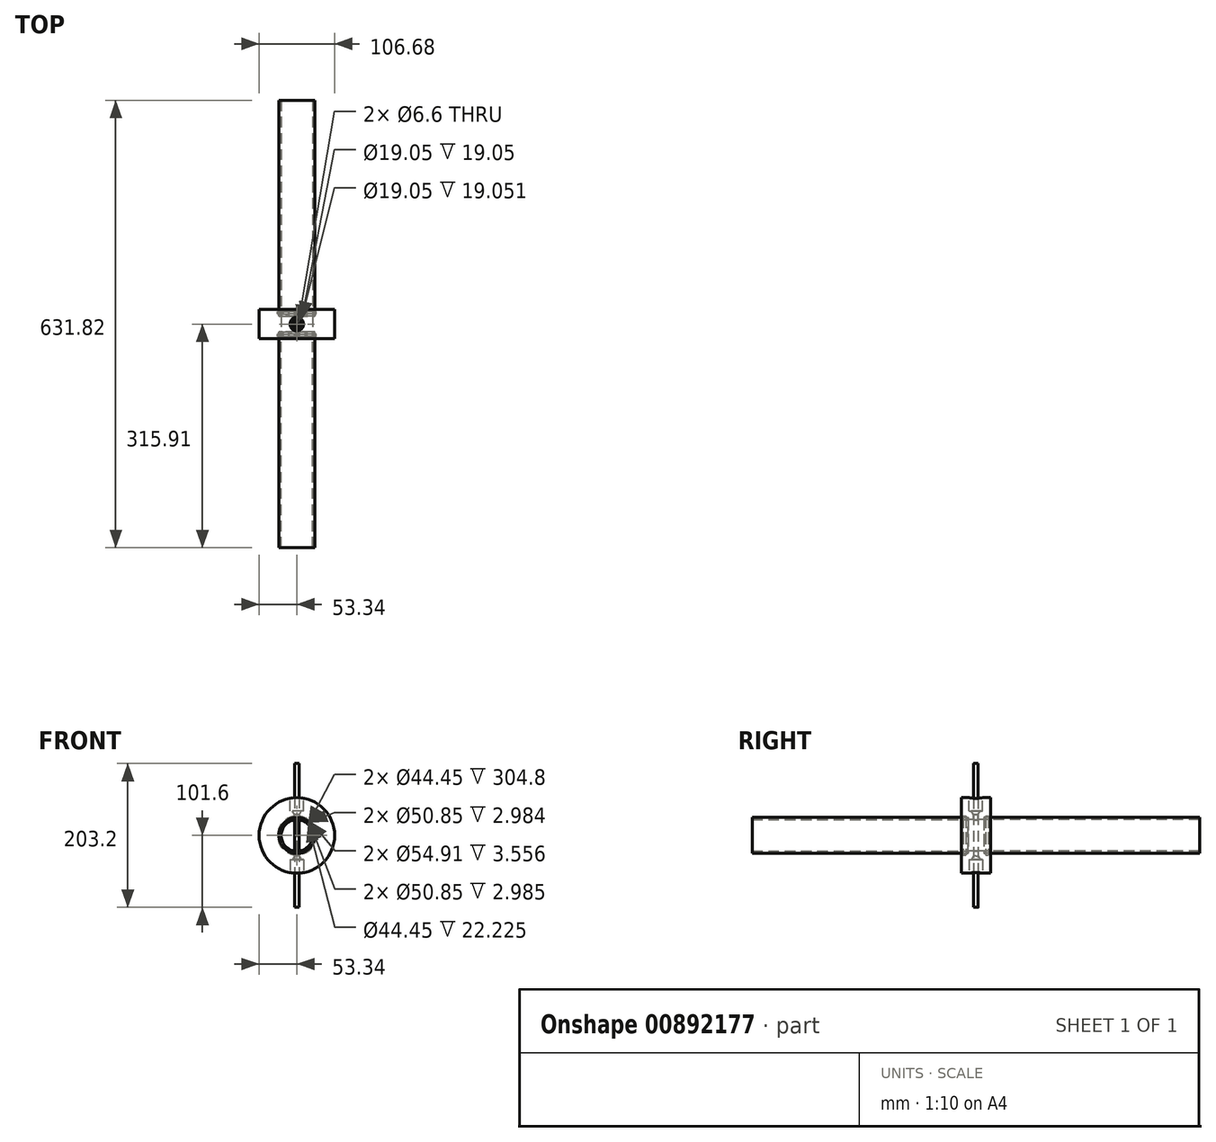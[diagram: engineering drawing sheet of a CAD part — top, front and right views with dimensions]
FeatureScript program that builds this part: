
annotation { "Feature Type Name" : "Feature", "Feature Type Description" : "" }
export const myFeature = defineFeature(function(context is Context, id is Id, definition is map)
    precondition{}
    {
        {
            var Q0;
            Q0=qCreatedBy(makeId("Front.planeOp"),FACE);
            var sketch = newSketch(context, id + "F0", { "sketchPlane" : qUnion([Q0])});
            skCircle(sketch, "E0", {"center": v(0, 0) * mm, "radius": 22.23 * mm});
            skCircle(sketch, "E1", {"center": v(0, 0) * mm, "radius": 53.34 * mm});
            skSolve(sketch);
        }
        {
            var Q0;
            Q0=makeQuery(id+"F0.imprint","IMPRINT",FACE,{"disambiguationData":[TD([[makeQuery(id+"F0.imprint","IMPRINT",EDGE,{"derivedFrom":sQuery(id+"F0.wireOp",EDGE,"E0")}),-1.0]])]});
            extrude(context, id + "F1", {"entities" : qUnion([Q0]), "oppositeDirection" : true, "depth" : 20.64 * mm, "offsetDistance" : 25.4 * mm});
        }
        {
            var Q0;
            Q0=qCreatedBy(makeId("Top.planeOp"),FACE);
            cPlane(context, id + "F2", {"entities" : qUnion([Q0]), "cplaneType" : CPlaneType.OFFSET, "offset" : 53.34 * mm, "width" : 152.4 * mm, "height" : 152.4 * mm});
        }
        {
            var Q0;
            Q0=qCreatedBy(makeId("Top.planeOp"),FACE);
            cPlane(context, id + "F3", {"entities" : qUnion([Q0]), "cplaneType" : CPlaneType.OFFSET, "offset" : 53.34 * mm, "oppositeDirection" : true, "width" : 152.4 * mm, "height" : 152.4 * mm});
        }
        {
            var Q0;
            Q0=qCreatedBy(id+"F2.planeOp",FACE);
            var sketch = newSketch(context, id + "F4", { "sketchPlane" : qUnion([Q0])});
            skCircle(sketch, "E2", {"center": v(0, 0) * mm, "radius": 9.53 * mm});
            skCircle(sketch, "E3", {"center": v(0, 0) * mm, "radius": 3.3 * mm});
            skSolve(sketch);
        }
        {
            var Q0;
            Q0=qCreatedBy(id+"F3.planeOp",FACE);
            var sketch = newSketch(context, id + "F5", { "sketchPlane" : qUnion([Q0])});
            skCircle(sketch, "E4", {"center": v(0, 0) * mm, "radius": 9.53 * mm});
            skCircle(sketch, "E5", {"center": v(0, 0) * mm, "radius": 3.3 * mm});
            skSolve(sketch);
        }
        {
            var Q0;
            Q0=makeQuery(id+"F0.imprint","IMPRINT",FACE,{"disambiguationData":[TD([[makeQuery(id+"F0.imprint","IMPRINT",EDGE,{"derivedFrom":sQuery(id+"F0.wireOp",EDGE,"E0")}),-1.0]])]});
            extrude(context, id + "F6", {"entities" : qUnion([Q0]), "operationType" : NewBodyOperationType.ADD, "depth" : 20.64 * mm, "offsetDistance" : 25.4 * mm});
        }
        {
            var Q0;
            Q0=makeQuery(id+"F5.imprint","IMPRINT",FACE,{"disambiguationData":[TD([[makeQuery(id+"F5.imprint","IMPRINT",EDGE,{"derivedFrom":sQuery(id+"F5.wireOp",EDGE,"E5")}),1.0]])]});
            var Q1;
            Q1=makeQuery(id+"F5.imprint","IMPRINT",FACE,{"disambiguationData":[TD([[makeQuery(id+"F5.imprint","IMPRINT",EDGE,{"derivedFrom":sQuery(id+"F5.wireOp",EDGE,"E4")}),1.0]])]});
            extrude(context, id + "F7", {"entities" : qUnion([Q0, Q1]), "operationType" : NewBodyOperationType.REMOVE, "depth" : 19.05 * mm, "offsetDistance" : 25.4 * mm});
        }
        {
            var Q0;
            Q0=makeQuery(id+"F5.imprint","IMPRINT",FACE,{"disambiguationData":[TD([[makeQuery(id+"F5.imprint","IMPRINT",EDGE,{"derivedFrom":sQuery(id+"F5.wireOp",EDGE,"E5")}),1.0]])]});
            var Q1;
            {var subQ0=sQuery(id+"F0.wireOp",EDGE,"E0");Q1=makeQuery(id+"F6.boolean.opBoolean","MERGE",FACE,{"derivedFrom":[makeQuery(id+"F1.opExtrude","SWEPT_FACE",FACE,{"disambiguationData":[OSD([subQ0])]}),makeQuery(id+"F6.opExtrude","SWEPT_FACE",FACE,{"disambiguationData":[OSD([subQ0])]})]});}
            extrude(context, id + "F8", {"entities" : qUnion([Q0]), "operationType" : NewBodyOperationType.REMOVE, "endBound" : BoundingType.UP_TO_SURFACE, "depth" : 25.4 * mm, "endBoundEntityFace" : qUnion([Q1]), "offsetDistance" : 25.4 * mm});
        }
        {
            var Q0;
            Q0=makeQuery(id+"F4.imprint","IMPRINT",FACE,{"disambiguationData":[TD([[makeQuery(id+"F4.imprint","IMPRINT",EDGE,{"derivedFrom":sQuery(id+"F4.wireOp",EDGE,"E2")}),1.0]])]});
            var Q1;
            Q1=makeQuery(id+"F4.imprint","IMPRINT",FACE,{"disambiguationData":[TD([[makeQuery(id+"F4.imprint","IMPRINT",EDGE,{"derivedFrom":sQuery(id+"F4.wireOp",EDGE,"E3")}),1.0]])]});
            extrude(context, id + "F9", {"entities" : qUnion([Q0, Q1]), "operationType" : NewBodyOperationType.REMOVE, "oppositeDirection" : true, "depth" : 19.05 * mm, "offsetDistance" : 25.4 * mm});
        }
        {
            var Q0;
            Q0=makeQuery(id+"F4.imprint","IMPRINT",FACE,{"disambiguationData":[TD([[makeQuery(id+"F4.imprint","IMPRINT",EDGE,{"derivedFrom":sQuery(id+"F4.wireOp",EDGE,"E3")}),1.0]])]});
            var Q1;
            {var subQ0=sQuery(id+"F0.wireOp",EDGE,"E0");Q1=makeQuery(id+"F6.boolean.opBoolean","MERGE",FACE,{"derivedFrom":[makeQuery(id+"F1.opExtrude","SWEPT_FACE",FACE,{"disambiguationData":[OSD([subQ0])]}),makeQuery(id+"F6.opExtrude","SWEPT_FACE",FACE,{"disambiguationData":[OSD([subQ0])]})]});}
            extrude(context, id + "F10", {"entities" : qUnion([Q0]), "operationType" : NewBodyOperationType.REMOVE, "endBound" : BoundingType.UP_TO_SURFACE, "oppositeDirection" : true, "depth" : 25.4 * mm, "endBoundEntityFace" : qUnion([Q1]), "offsetDistance" : 25.4 * mm});
        }
        {
            var Q0;
            Q0=qCreatedBy(makeId("Right.planeOp"),FACE);
            var sketch = newSketch(context, id + "F11", { "sketchPlane" : qUnion([Q0])});
            skLineSegment(sketch, "E6", {"start": v(0, 0) * mm, "end": v(3.3, 0) * mm});
            skLineSegment(sketch, "E7", {"start": v(3.3, 34.3) * mm, "end": v(6.35, 34.3) * mm});
            skLineSegment(sketch, "E8", {"start": v(3.3, 29.21) * mm, "end": v(6.35, 34.3) * mm});
            skLineSegment(sketch, "E9", {"start": v(3.3, -34.3) * mm, "end": v(6.35, -34.3) * mm});
            skLineSegment(sketch, "E10", {"start": v(3.3, -29.21) * mm, "end": v(6.35, -34.3) * mm});
            skLineSegment(sketch, "E11", {"start": v(0, 0) * mm, "end": v(0, 13.94) * mm});
            skLineSegment(sketch, "E12", {"start": v(0, 13.94) * mm, "end": v(0, -17.8) * mm});
            skLineSegment(sketch, "E13", {"start": v(3.3, 34.3) * mm, "end": v(3.3, 29.21) * mm});
            skLineSegment(sketch, "E14", {"start": v(3.3, -29.21) * mm, "end": v(3.3, -34.3) * mm});
            skSolve(sketch);
        }
        {
            var Q0;
            Q0 = qSketchRegion(id + "F11", true);
            var Q1;
            Q1=sQuery(id+"F11.wireOp",EDGE,"E11");
            revolve(context, id + "F12", {"operationType" : NewBodyOperationType.REMOVE, "surfaceOperationType" : NewSurfaceOperationType.NEW, "entities" : qUnion([Q0]), "axis" : qUnion([Q1]), "revolveType" : RevolveType.FULL, "oppositeDirection" : true});
        }
        {
            var Q0;
            Q0=qCreatedBy(makeId("Top.planeOp"),FACE);
            var sketch = newSketch(context, id + "F13", { "sketchPlane" : qUnion([Q0])});
            skLineSegment(sketch, "E15", {"start": v(0, 0) * mm, "end": v(0, 11.11) * mm});
            skLineSegment(sketch, "E16", {"start": v(0, 11.11) * mm, "end": v(-22.23, 11.11) * mm});
            skLineSegment(sketch, "E17", {"start": v(-22.23, 11.11) * mm, "end": v(-22.23, 20.64) * mm});
            skLineSegment(sketch, "E18", {"start": v(-22.23, 20.64) * mm, "end": v(-25.43, 20.64) * mm});
            skLineSegment(sketch, "E19", {"start": v(-25.43, 20.64) * mm, "end": v(-25.43, 11.11) * mm});
            skLineSegment(sketch, "E20", {"start": v(-25.43, 11.11) * mm, "end": v(-22.23, 11.11) * mm});
            skLineSegment(sketch, "E21", {"start": v(-27.46, 14.1) * mm, "end": v(-25.43, 14.1) * mm});
            skLineSegment(sketch, "E22", {"start": v(-27.46, 14.1) * mm, "end": v(-27.46, 17.65) * mm});
            skLineSegment(sketch, "E23", {"start": v(-27.46, 17.65) * mm, "end": v(-25.43, 17.65) * mm});
            skLineSegment(sketch, "E24", {"start": v(-10.88, 0) * mm, "end": v(12, 0) * mm, "construction": true});
            skLineSegment(sketch, "E25.MirrorCS", {"start": v(0, 0) * mm, "end": v(0, -11.11) * mm});
            skLineSegment(sketch, "E26.MirrorCS", {"start": v(0, -11.11) * mm, "end": v(-22.23, -11.11) * mm});
            skLineSegment(sketch, "E27.MirrorCS", {"start": v(-25.43, -11.11) * mm, "end": v(-22.23, -11.11) * mm});
            skLineSegment(sketch, "E28.MirrorCS", {"start": v(-25.43, -20.64) * mm, "end": v(-25.43, -11.11) * mm});
            skLineSegment(sketch, "E29.MirrorCS", {"start": v(-27.46, -14.1) * mm, "end": v(-25.43, -14.1) * mm});
            skLineSegment(sketch, "E30.MirrorCS", {"start": v(-27.46, -14.1) * mm, "end": v(-27.46, -17.65) * mm});
            skLineSegment(sketch, "E31.MirrorCS", {"start": v(-27.46, -17.65) * mm, "end": v(-25.43, -17.65) * mm});
            skLineSegment(sketch, "E32.MirrorCS", {"start": v(-22.23, -20.64) * mm, "end": v(-25.43, -20.64) * mm});
            skLineSegment(sketch, "E33.MirrorCS", {"start": v(-22.23, -11.11) * mm, "end": v(-22.23, -20.64) * mm});
            skSolve(sketch);
        }
        {
            var Q0;
            Q0 = qSketchRegion(id + "F13", true);
            var Q1;
            Q1=sQuery(id+"F13.wireOp",EDGE,"E15");
            revolve(context, id + "F14", {"operationType" : NewBodyOperationType.REMOVE, "surfaceOperationType" : NewSurfaceOperationType.NEW, "entities" : qUnion([Q0]), "axis" : qUnion([Q1]), "revolveType" : RevolveType.FULL, "oppositeDirection" : true});
        }
        {
            var Q0;
            Q0=qCreatedBy(makeId("Top.planeOp"),FACE);
            var sketch = newSketch(context, id + "F15", { "sketchPlane" : qUnion([Q0])});
            skCircle(sketch, "E34", {"center": v(0, 0) * mm, "radius": 3.18 * mm});
            skSolve(sketch);
        }
        {
            var Q0;
            Q0=makeQuery(id+"F15.imprint","IMPRINT",FACE,{"disambiguationData":[TD([[makeQuery(id+"F15.imprint","IMPRINT",EDGE,{"derivedFrom":sQuery(id+"F15.wireOp",EDGE,"E34")}),1.0]])]});
            extrude(context, id + "F16", {"entities" : qUnion([Q0]), "endBound" : BoundingType.SYMMETRIC, "depth" : 203.2 * mm, "offsetDistance" : 25.4 * mm});
        }
        {
            var Q0;
            Q0=qCreatedBy(makeId("Top.planeOp"),FACE);
            var sketch = newSketch(context, id + "F17", { "sketchPlane" : qUnion([Q0])});
            skLineSegment(sketch, "E35", {"start": v(0, 0) * mm, "end": v(0, 18.94) * mm, "construction": true});
            skCircle(sketch, "E36", {"center": v(-25.9, 15.88) * mm, "radius": 1.52 * mm});
            skLineSegment(sketch, "E37", {"start": v(-12.45, 0) * mm, "end": v(12.9, 0) * mm, "construction": true});
            skCircle(sketch, "E38.MirrorC", {"center": v(-25.9, -15.88) * mm, "radius": 1.52 * mm});
            skSolve(sketch);
        }
        {
            var Q0;
            Q0=sQuery(id+"F17.wireOp",EDGE,"E36");
            var Q1;
            Q1=sQuery(id+"F17.wireOp",EDGE,"E38.MirrorC");
            var Q2;
            Q2=sQuery(id+"F17.wireOp",EDGE,"E35");
            revolve(context, id + "F18", {"bodyType" : ToolBodyType.SURFACE, "surfaceOperationType" : NewSurfaceOperationType.NEW, "surfaceEntities" : qUnion([Q0, Q1]), "axis" : qUnion([Q2]), "revolveType" : RevolveType.FULL});
        }
        {
            var Q0;
            Q0=makeQuery(id+"F14.boolean.opBoolean","COPY",FACE,{"derivedFrom":makeQuery(id+"F14.opRevolve","SWEPT_FACE",FACE,{"disambiguationData":[OSD([sQuery(id+"F13.wireOp",EDGE,"E27.MirrorCS")])]})});
            var sketch = newSketch(context, id + "F19", { "sketchPlane" : qUnion([Q0])});
            skCircle(sketch, "E39", {"center": v(0, 0) * mm, "radius": 25.4 * mm});
            skCircle(sketch, "E40", {"center": v(0, 0) * mm, "radius": 22.23 * mm});
            skSolve(sketch);
        }
        {
            var Q0;
            Q0 = qSketchRegion(id + "F19", true);
            extrude(context, id + "F20", {"entities" : qUnion([Q0]), "depth" : 304.8 * mm, "offsetDistance" : 25.4 * mm});
        }
        {
            var Q0;
            Q0=makeQuery(id+"F14.boolean.opBoolean","COPY",FACE,{"derivedFrom":makeQuery(id+"F14.opRevolve","SWEPT_FACE",FACE,{"disambiguationData":[OSD([sQuery(id+"F13.wireOp",EDGE,"E20")])]})});
            var sketch = newSketch(context, id + "F21", { "sketchPlane" : qUnion([Q0])});
            skCircle(sketch, "E41", {"center": v(0, 0) * mm, "radius": 25.4 * mm});
            skCircle(sketch, "E42", {"center": v(0, 0) * mm, "radius": 22.23 * mm});
            skSolve(sketch);
        }
        {
            var Q0;
            Q0 = qSketchRegion(id + "F21", true);
            extrude(context, id + "F22", {"entities" : qUnion([Q0]), "depth" : 304.8 * mm, "offsetDistance" : 25.4 * mm});
        }
    });
